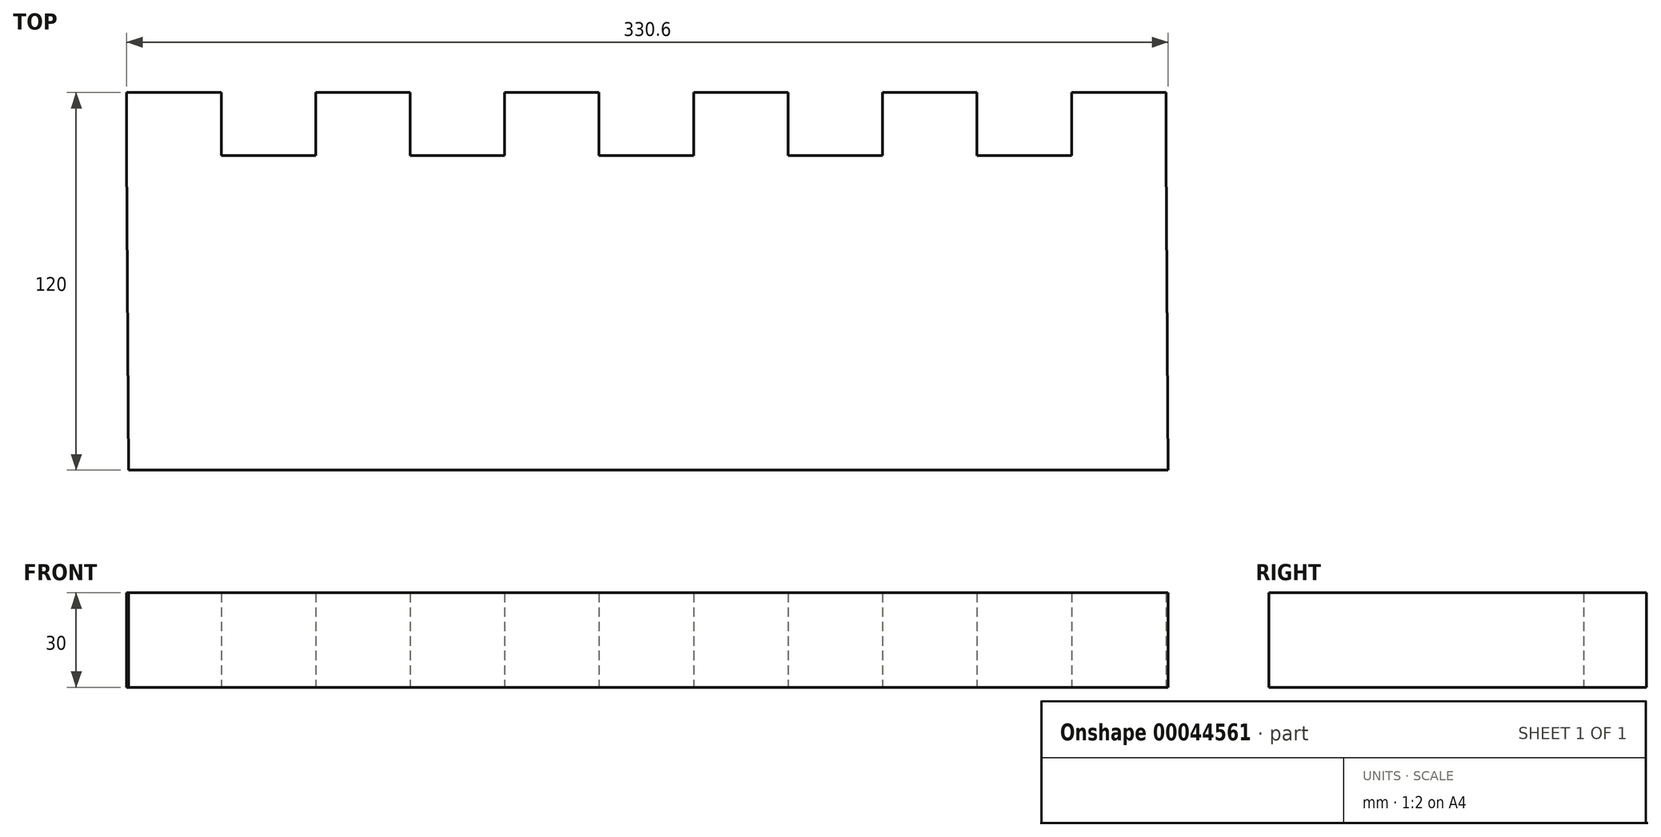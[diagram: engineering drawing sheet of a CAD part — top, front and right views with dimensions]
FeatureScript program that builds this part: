
annotation { "Feature Type Name" : "Feature", "Feature Type Description" : "" }
export const myFeature = defineFeature(function(context is Context, id is Id, definition is map)
    precondition{}
    {
        {
            var Q0;
            Q0=qCreatedBy(makeId("Top.planeOp"),FACE);
            var sketch = newSketch(context, id + "F0", { "sketchPlane" : qUnion([Q0])});
            skLineSegment(sketch, "E0", {"start": v(0, 0) * mm, "end": v(0.6, -100) * mm});
            skLineSegment(sketch, "E1", {"start": v(0.6, -100) * mm, "end": v(330.6, -100) * mm});
            skLineSegment(sketch, "E2", {"start": v(300, 0) * mm, "end": v(270, 0) * mm});
            skLineSegment(sketch, "E3", {"start": v(0, 0) * mm, "end": v(0, 20) * mm});
            skLineSegment(sketch, "E4", {"start": v(0, 20) * mm, "end": v(30, 20) * mm});
            skLineSegment(sketch, "E5", {"start": v(30, 20) * mm, "end": v(30, 0) * mm});
            skLineSegment(sketch, "E6", {"start": v(30, 0) * mm, "end": v(60, 0) * mm});
            skLineSegment(sketch, "E7", {"start": v(60, 0) * mm, "end": v(60, 20) * mm});
            skLineSegment(sketch, "E8", {"start": v(60, 20) * mm, "end": v(90, 20) * mm});
            skLineSegment(sketch, "E9", {"start": v(90, 20) * mm, "end": v(90, 0) * mm});
            skLineSegment(sketch, "E10", {"start": v(90, 0) * mm, "end": v(120, 0) * mm});
            skLineSegment(sketch, "E11", {"start": v(120, 0) * mm, "end": v(120, 20) * mm});
            skLineSegment(sketch, "E12", {"start": v(120, 20) * mm, "end": v(150, 20) * mm});
            skLineSegment(sketch, "E13", {"start": v(150, 20) * mm, "end": v(150, 0) * mm});
            skLineSegment(sketch, "E14", {"start": v(222.48, 0) * mm, "end": v(240, 0) * mm});
            skLineSegment(sketch, "E15", {"start": v(150, 0) * mm, "end": v(180, 0) * mm});
            skLineSegment(sketch, "E16", {"start": v(180, 0) * mm, "end": v(180, 20) * mm});
            skLineSegment(sketch, "E17", {"start": v(180, 20) * mm, "end": v(210, 20) * mm});
            skLineSegment(sketch, "E18", {"start": v(210, 20) * mm, "end": v(210, 0) * mm});
            skLineSegment(sketch, "E19", {"start": v(210, 0) * mm, "end": v(240, 0) * mm});
            skLineSegment(sketch, "E20", {"start": v(240, 0) * mm, "end": v(240, 20) * mm});
            skLineSegment(sketch, "E21", {"start": v(240, 20) * mm, "end": v(270, 20) * mm});
            skLineSegment(sketch, "E22", {"start": v(270, 20) * mm, "end": v(270, 0) * mm});
            skLineSegment(sketch, "E23", {"start": v(270, 0) * mm, "end": v(300, 0) * mm});
            skLineSegment(sketch, "E24", {"start": v(300, 0) * mm, "end": v(300, 20) * mm});
            skLineSegment(sketch, "E25", {"start": v(300, 20) * mm, "end": v(330, 20) * mm});
            skLineSegment(sketch, "E26", {"start": v(330, 20) * mm, "end": v(330, 0) * mm});
            skLineSegment(sketch, "E27.trimOffspring", {"start": v(120, 0) * mm, "end": v(90, 0) * mm});
            skLineSegment(sketch, "E28.trimOffspring", {"start": v(180, 0) * mm, "end": v(150, 0) * mm});
            skLineSegment(sketch, "E29.trimOffspring", {"start": v(240, 0) * mm, "end": v(210, 0) * mm});
            skLineSegment(sketch, "E30.trimOffspring", {"start": v(60, 0) * mm, "end": v(30, 0) * mm});
            skLineSegment(sketch, "E31", {"start": v(330.6, -100) * mm, "end": v(330, 0) * mm});
            skSolve(sketch);
        }
        {
            var Q0;
            Q0 = qSketchRegion(id + "F0", true);
            extrude(context, id + "F1", {"entities" : qUnion([Q0]), "depth" : 30 * mm});
        }
    });
